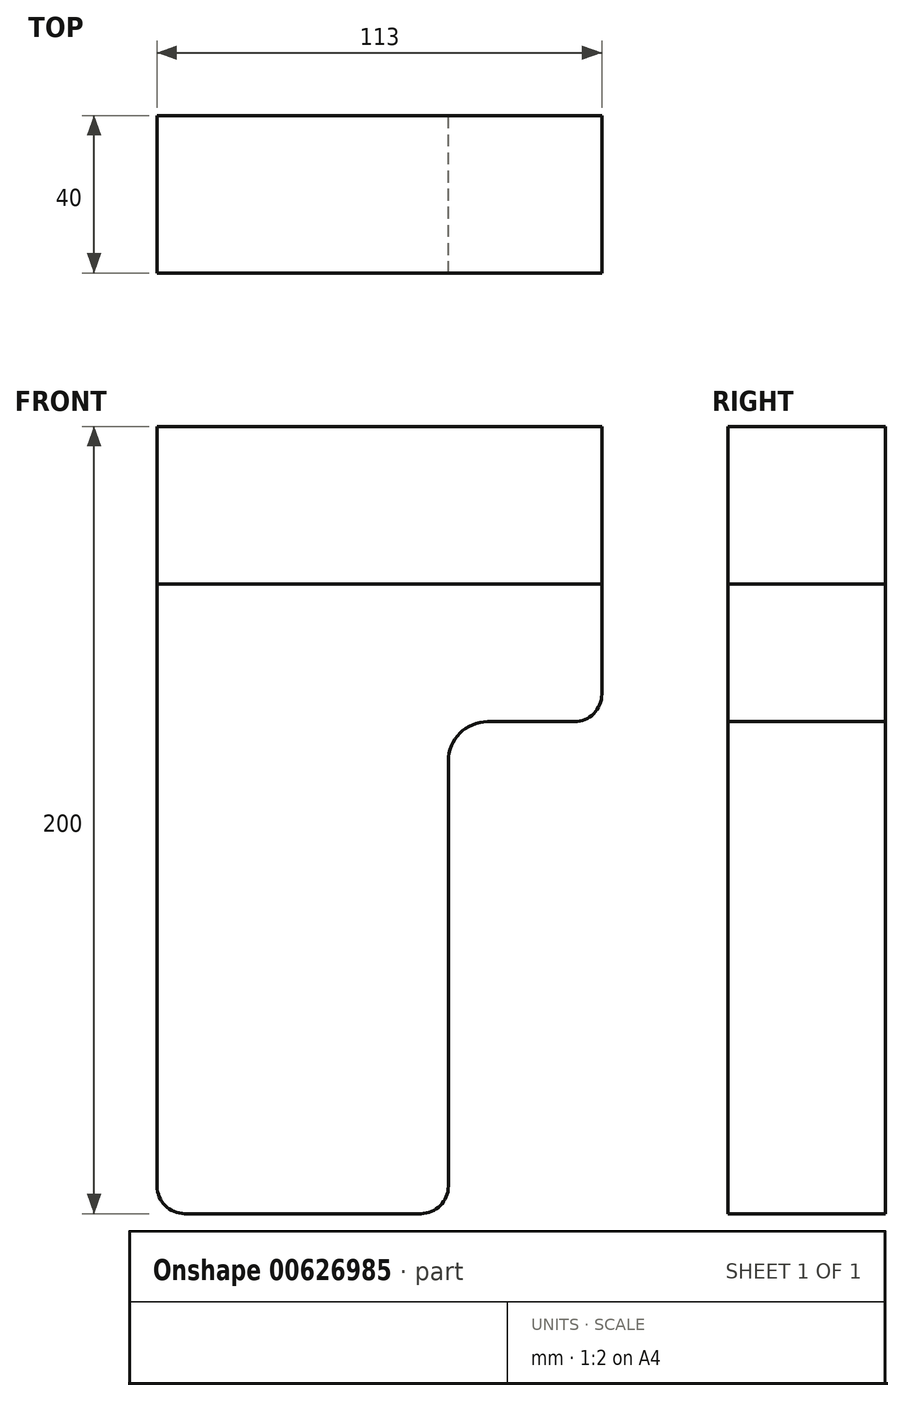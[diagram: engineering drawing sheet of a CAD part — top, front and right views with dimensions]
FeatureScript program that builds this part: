
annotation { "Feature Type Name" : "Feature", "Feature Type Description" : "" }
export const myFeature = defineFeature(function(context is Context, id is Id, definition is map)
    precondition{}
    {
        {
            var Q0;
            Q0=qCreatedBy(makeId("Front.planeOp"),FACE);
            var sketch = newSketch(context, id + "F0", { "sketchPlane" : qUnion([Q0])});
            skLineSegment(sketch, "E0.bottom", {"start": v(0, 0) * mm, "end": v(74, 0) * mm});
            skLineSegment(sketch, "E0.top", {"start": v(0, 160) * mm, "end": v(113, 160) * mm});
            skLineSegment(sketch, "E0.left", {"start": v(0, 0) * mm, "end": v(0, 160) * mm});
            skLineSegment(sketch, "E0.right", {"start": v(113, 125) * mm, "end": v(113, 160) * mm});
            skLineSegment(sketch, "E1", {"start": v(74, 0) * mm, "end": v(74, 125) * mm});
            skLineSegment(sketch, "E2", {"start": v(74, 125) * mm, "end": v(113, 125) * mm});
            skSolve(sketch);
        }
        {
            var Q0;
            Q0=makeQuery(id+"F0.imprint","IMPRINT",FACE,{"disambiguationData":[TD([[makeQuery(id+"F0.imprint","IMPRINT",EDGE,{"derivedFrom":sQuery(id+"F0.wireOp",EDGE,"E0.bottom")}),1.0]])]});
            extrude(context, id + "F1", {"entities" : qUnion([Q0]), "endBound" : BoundingType.SYMMETRIC, "depth" : 46 * mm, "offsetDistance" : 25 * mm});
        }
        {
            var Q0;
            Q0=makeQuery(id+"F1.opExtrude","SWEPT_FACE",FACE,{"disambiguationData":[OSD([sQuery(id+"F0.wireOp",EDGE,"E0.top")])]});
            var sketch = newSketch(context, id + "F2", { "sketchPlane" : qUnion([Q0])});
            skSolve(sketch);
        }
        {
            var Q0;
            Q0 = qSketchRegion(id + "F2", true);
            var Q1;
            {var subQ0=sQuery(id+"F0.wireOp",EDGE,"E0.top");Q1=makeQuery(id+"F2.imprint","IMPRINT",FACE,{"disambiguationData":[TD([[makeQuery(id+"F2.imprint","IMPRINT",EDGE,{"derivedFrom":makeQuery(id+"F1.opExtrude","CAP_EDGE",EDGE,{"disambiguationData":[OSD([subQ0])],"isStart":true})}),-1.0]])]});}
            extrude(context, id + "F3", {"entities" : qUnion([Q0, Q1]), "depth" : 40 * mm, "offsetDistance" : 25 * mm});
        }
        {
            var Q0;
            Q0=makeQuery(id+"F1.opExtrude","SWEPT_EDGE",EDGE,{"disambiguationData":[OSD([sQuery(id+"F0.wireOp",EDGE,"E0.bottom"),sQuery(id+"F0.wireOp",EDGE,"E1")])]});
            var Q1;
            Q1=makeQuery(id+"F1.opExtrude","SWEPT_EDGE",EDGE,{"disambiguationData":[OSD([sQuery(id+"F0.wireOp",EDGE,"E0.bottom"),sQuery(id+"F0.wireOp",EDGE,"E0.left")])]});
            var Q2;
            Q2=makeQuery(id+"F1.opExtrude","SWEPT_EDGE",EDGE,{"disambiguationData":[OSD([sQuery(id+"F0.wireOp",EDGE,"E0.right"),sQuery(id+"F0.wireOp",EDGE,"E2")])]});
            fillet(context, id + "F4", {"entities" : qUnion([Q0, Q1, Q2]), "radius" : 7 * mm, "tangentPropagation" : true, "allowEdgeOverflow" : false});
        }
        {
            var Q0;
            Q0=makeQuery(id+"F1.opExtrude","SWEPT_EDGE",EDGE,{"disambiguationData":[OSD([sQuery(id+"F0.wireOp",EDGE,"E1"),sQuery(id+"F0.wireOp",EDGE,"E2")])]});
            fillet(context, id + "F5", {"entities" : qUnion([Q0]), "radius" : 10 * mm, "tangentPropagation" : true, "allowEdgeOverflow" : false});
        }
        {
            var Q0;
            Q0=makeQuery(id+"F3.opExtrude","CAP_FACE",FACE,{"disambiguationData":[OSD([sQuery(id+"F0.wireOp",EDGE,"E0.top"),sQuery(id+"F0.wireOp",EDGE,"E0.left"),sQuery(id+"F0.wireOp",EDGE,"E0.right")])],"isStart":false});
            var sketch = newSketch(context, id + "F6", { "sketchPlane" : qUnion([Q0])});
            skLineSegment(sketch, "E3.bottom", {"start": v(0, 23) * mm, "end": v(113, 23) * mm});
            skLineSegment(sketch, "E3.top", {"start": v(0, 17) * mm, "end": v(113, 17) * mm});
            skLineSegment(sketch, "E3.left", {"start": v(0, 23) * mm, "end": v(0, 17) * mm});
            skLineSegment(sketch, "E3.right", {"start": v(113, 23) * mm, "end": v(113, 17) * mm});
            skLineSegment(sketch, "E4.top", {"start": v(0, -23) * mm, "end": v(113, -23) * mm});
            skLineSegment(sketch, "E4.left", {"start": v(0, 17) * mm, "end": v(0, -23) * mm});
            skLineSegment(sketch, "E4.right", {"start": v(113, 17) * mm, "end": v(113, -23) * mm});
            skSolve(sketch);
        }
        {
            var Q0;
            Q0=makeQuery(id+"F6.imprint","IMPRINT",FACE,{"disambiguationData":[TD([[makeQuery(id+"F6.imprint","IMPRINT",EDGE,{"derivedFrom":sQuery(id+"F6.wireOp",EDGE,"E3.bottom")}),-1.0]])]});
            extrude(context, id + "F7", {"entities" : qUnion([Q0]), "operationType" : NewBodyOperationType.REMOVE, "endBound" : BoundingType.THROUGH_ALL, "oppositeDirection" : true, "depth" : 25 * mm, "offsetDistance" : 25 * mm});
        }
    });
